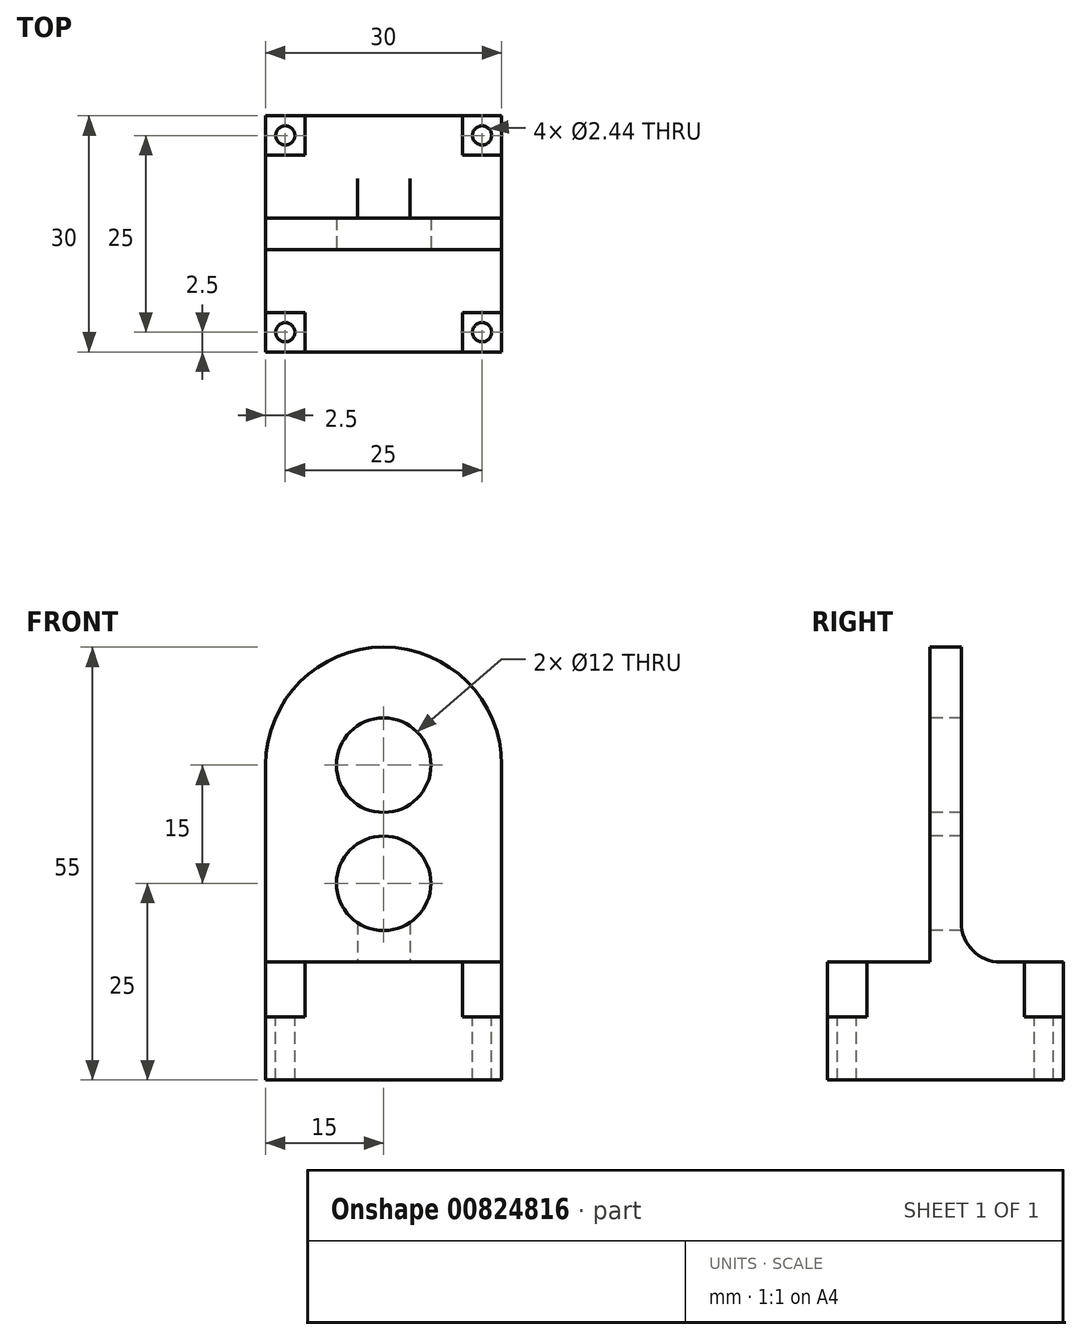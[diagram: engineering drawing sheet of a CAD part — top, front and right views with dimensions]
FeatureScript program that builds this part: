
annotation { "Feature Type Name" : "Feature", "Feature Type Description" : "" }
export const myFeature = defineFeature(function(context is Context, id is Id, definition is map)
    precondition{}
    {
        {
            var Q0;
            Q0=qCreatedBy(makeId("Top.planeOp"),FACE);
            var sketch = newSketch(context, id + "F0", { "sketchPlane" : qUnion([Q0])});
            skLineSegment(sketch, "E0.bottom", {"start": v(15, -15) * mm, "end": v(-15, -15) * mm});
            skLineSegment(sketch, "E0.top", {"start": v(15, 15) * mm, "end": v(-15, 15) * mm});
            skLineSegment(sketch, "E0.left", {"start": v(15, -15) * mm, "end": v(15, 15) * mm});
            skLineSegment(sketch, "E0.right", {"start": v(-15, -15) * mm, "end": v(-15, 15) * mm});
            skPoint(sketch, "E0.middle", {"position": v(0, 0) * mm});
            skSolve(sketch);
        }
        {
            var Q0;
            Q0=makeQuery(id+"F0.imprint","IMPRINT",FACE,{"disambiguationData":[TD([[makeQuery(id+"F0.imprint","IMPRINT",EDGE,{"derivedFrom":sQuery(id+"F0.wireOp",EDGE,"E0.bottom")}),-1.0]])]});
            extrude(context, id + "F1", {"entities" : qUnion([Q0]), "depth" : 15 * mm, "offsetDistance" : 25 * mm});
        }
        {
            var Q0;
            Q0=makeQuery(id+"F1.opExtrude","CAP_FACE",FACE,{"disambiguationData":[OSD([sQuery(id+"F0.wireOp",EDGE,"E0.bottom"),sQuery(id+"F0.wireOp",EDGE,"E0.top"),sQuery(id+"F0.wireOp",EDGE,"E0.left"),sQuery(id+"F0.wireOp",EDGE,"E0.right")])],"isStart":false});
            var sketch = newSketch(context, id + "F2", { "sketchPlane" : qUnion([Q0])});
            skLineSegment(sketch, "E1.bottom", {"start": v(-15, 15) * mm, "end": v(-10, 15) * mm});
            skLineSegment(sketch, "E1.top", {"start": v(-15, 10) * mm, "end": v(-10, 10) * mm});
            skLineSegment(sketch, "E1.left", {"start": v(-15, 15) * mm, "end": v(-15, 10) * mm});
            skLineSegment(sketch, "E1.right", {"start": v(-10, 15) * mm, "end": v(-10, 10) * mm});
            skLineSegment(sketch, "E2.bottom", {"start": v(15, 15) * mm, "end": v(10, 15) * mm});
            skLineSegment(sketch, "E2.top", {"start": v(15, 10) * mm, "end": v(10, 10) * mm});
            skLineSegment(sketch, "E2.left", {"start": v(15, 15) * mm, "end": v(15, 10) * mm});
            skLineSegment(sketch, "E2.right", {"start": v(10, 15) * mm, "end": v(10, 10) * mm});
            skLineSegment(sketch, "E3.bottom", {"start": v(15, -15) * mm, "end": v(10, -15) * mm});
            skLineSegment(sketch, "E3.top", {"start": v(15, -10) * mm, "end": v(10, -10) * mm});
            skLineSegment(sketch, "E3.left", {"start": v(15, -15) * mm, "end": v(15, -10) * mm});
            skLineSegment(sketch, "E3.right", {"start": v(10, -15) * mm, "end": v(10, -10) * mm});
            skLineSegment(sketch, "E4.bottom", {"start": v(-15, -15) * mm, "end": v(-10, -15) * mm});
            skLineSegment(sketch, "E4.top", {"start": v(-15, -10) * mm, "end": v(-10, -10) * mm});
            skLineSegment(sketch, "E4.left", {"start": v(-15, -15) * mm, "end": v(-15, -10) * mm});
            skLineSegment(sketch, "E4.right", {"start": v(-10, -15) * mm, "end": v(-10, -10) * mm});
            skSolve(sketch);
        }
        {
            var Q0;
            Q0=makeQuery(id+"F2.imprint","IMPRINT",FACE,{"disambiguationData":[TD([[makeQuery(id+"F2.imprint","IMPRINT",EDGE,{"derivedFrom":sQuery(id+"F2.wireOp",EDGE,"E1.bottom")}),1.0]])]});
            var Q1;
            Q1=makeQuery(id+"F2.imprint","IMPRINT",FACE,{"disambiguationData":[TD([[makeQuery(id+"F2.imprint","IMPRINT",EDGE,{"derivedFrom":sQuery(id+"F2.wireOp",EDGE,"E2.bottom")}),1.0]])]});
            var Q2;
            Q2=makeQuery(id+"F2.imprint","IMPRINT",FACE,{"disambiguationData":[TD([[makeQuery(id+"F2.imprint","IMPRINT",EDGE,{"derivedFrom":sQuery(id+"F2.wireOp",EDGE,"E3.bottom")}),-1.0]])]});
            var Q3;
            Q3=makeQuery(id+"F2.imprint","IMPRINT",FACE,{"disambiguationData":[TD([[makeQuery(id+"F2.imprint","IMPRINT",EDGE,{"derivedFrom":sQuery(id+"F2.wireOp",EDGE,"E4.bottom")}),-1.0]])]});
            extrude(context, id + "F3", {"entities" : qUnion([Q0, Q1, Q2, Q3]), "operationType" : NewBodyOperationType.REMOVE, "oppositeDirection" : true, "depth" : 7 * mm, "offsetDistance" : 25 * mm});
        }
        {
            var Q0;
            Q0=makeQuery(id+"F3.boolean.opBoolean","COPY",FACE,{"derivedFrom":makeQuery(id+"F3.opExtrude","CAP_FACE",FACE,{"disambiguationData":[OSD([sQuery(id+"F2.wireOp",EDGE,"E1.bottom"),sQuery(id+"F2.wireOp",EDGE,"E1.top"),sQuery(id+"F2.wireOp",EDGE,"E1.left"),sQuery(id+"F2.wireOp",EDGE,"E1.right")])],"isStart":false})});
            var sketch = newSketch(context, id + "F4", { "sketchPlane" : qUnion([Q0])});
            skCircle(sketch, "E5", {"center": v(-12.5, 12.5) * mm, "radius": 1.22 * mm});
            skPoint(sketch, "E5.centerSnap0", {"position": v(-12.5, 15) * mm});
            skPoint(sketch, "E5.centerSnap1", {"position": v(-15, 12.5) * mm});
            skCircle(sketch, "E6.1.0", {"center": v(-12.5, -12.5) * mm, "radius": 1.22 * mm});
            skCircle(sketch, "E6.2.0", {"center": v(12.5, -12.5) * mm, "radius": 1.22 * mm});
            skCircle(sketch, "E6.3.0", {"center": v(12.5, 12.5) * mm, "radius": 1.22 * mm});
            skPoint(sketch, "E6.center", {"position": v(0, 0) * mm});
            skSolve(sketch);
        }
        {
            var Q0;
            Q0=makeQuery(id+"F4.imprint","IMPRINT",FACE,{"disambiguationData":[TD([[makeQuery(id+"F4.imprint","IMPRINT",EDGE,{"derivedFrom":sQuery(id+"F4.wireOp",EDGE,"E5")}),1.0]])]});
            var Q1;
            Q1=makeQuery(id+"F4.imprint","IMPRINT",FACE,{"disambiguationData":[TD([[makeQuery(id+"F4.imprint","IMPRINT",EDGE,{"derivedFrom":sQuery(id+"F4.wireOp",EDGE,"E6.3.0")}),1.0]])]});
            var Q2;
            Q2=makeQuery(id+"F4.imprint","IMPRINT",FACE,{"disambiguationData":[TD([[makeQuery(id+"F4.imprint","IMPRINT",EDGE,{"derivedFrom":sQuery(id+"F4.wireOp",EDGE,"E6.2.0")}),1.0]])]});
            var Q3;
            Q3=makeQuery(id+"F4.imprint","IMPRINT",FACE,{"disambiguationData":[TD([[makeQuery(id+"F4.imprint","IMPRINT",EDGE,{"derivedFrom":sQuery(id+"F4.wireOp",EDGE,"E6.1.0")}),1.0]])]});
            extrude(context, id + "F5", {"entities" : qUnion([Q0, Q1, Q2, Q3]), "operationType" : NewBodyOperationType.REMOVE, "endBound" : BoundingType.THROUGH_ALL, "oppositeDirection" : true, "depth" : 25 * mm, "offsetDistance" : 25 * mm});
        }
        {
            var Q0;
            Q0=qCreatedBy(makeId("Front.planeOp"),FACE);
            var sketch = newSketch(context, id + "F6", { "sketchPlane" : qUnion([Q0])});
            skLineSegment(sketch, "E7.bottom", {"start": v(-15, 15) * mm, "end": v(15, 15) * mm});
            skLineSegment(sketch, "E7.top", {"start": v(0, 55) * mm, "end": v(0, 55) * mm});
            skLineSegment(sketch, "E7.left", {"start": v(-15, 15) * mm, "end": v(-15, 40) * mm});
            skLineSegment(sketch, "E7.right", {"start": v(15, 15) * mm, "end": v(15, 40) * mm});
            skPoint(sketch, "E8.visualSharp", {"position": v(-15, 55) * mm});
            skArc(sketch, "E8.filletArc", {"start": v(0, 55) * mm, "mid": v(-10.6, 50.6) * mm, "end": v(-15, 40) * mm});
            skPoint(sketch, "E9.visualSharp", {"position": v(15, 55) * mm});
            skArc(sketch, "E9.filletArc", {"start": v(15, 40) * mm, "mid": v(10.6, 50.6) * mm, "end": v(0, 55) * mm});
            skSolve(sketch);
        }
        {
            var Q0;
            Q0=makeQuery(id+"F6.imprint","IMPRINT",FACE,{"disambiguationData":[TD([[makeQuery(id+"F6.imprint","IMPRINT",EDGE,{"derivedFrom":sQuery(id+"F6.wireOp",EDGE,"E7.bottom")}),1.0]])]});
            extrude(context, id + "F7", {"entities" : qUnion([Q0]), "operationType" : NewBodyOperationType.ADD, "endBound" : BoundingType.SYMMETRIC, "depth" : 4 * mm, "offsetDistance" : 25 * mm});
        }
        {
            var Q0;
            Q0=makeQuery(id+"F7.opExtrude","CAP_FACE",FACE,{"disambiguationData":[OSD([sQuery(id+"F6.wireOp",EDGE,"E7.bottom"),sQuery(id+"F6.wireOp",EDGE,"E7.left"),sQuery(id+"F6.wireOp",EDGE,"E7.right"),sQuery(id+"F6.wireOp",EDGE,"E8.filletArc"),sQuery(id+"F6.wireOp",EDGE,"E9.filletArc")])],"isStart":false});
            var sketch = newSketch(context, id + "F8", { "sketchPlane" : qUnion([Q0])});
            skCircle(sketch, "E10", {"center": v(0, 40) * mm, "radius": 6 * mm});
            skCircle(sketch, "E11", {"center": v(0, 25) * mm, "radius": 6 * mm});
            skSolve(sketch);
        }
        {
            var Q0;
            Q0=makeQuery(id+"F8.imprint","IMPRINT",FACE,{"disambiguationData":[TD([[makeQuery(id+"F8.imprint","IMPRINT",EDGE,{"derivedFrom":sQuery(id+"F8.wireOp",EDGE,"E10")}),1.0]])]});
            var Q1;
            Q1=makeQuery(id+"F8.imprint","IMPRINT",FACE,{"disambiguationData":[TD([[makeQuery(id+"F8.imprint","IMPRINT",EDGE,{"derivedFrom":sQuery(id+"F8.wireOp",EDGE,"E11")}),1.0]])]});
            extrude(context, id + "F9", {"entities" : qUnion([Q0, Q1]), "operationType" : NewBodyOperationType.REMOVE, "endBound" : BoundingType.THROUGH_ALL, "oppositeDirection" : true, "depth" : 25 * mm, "offsetDistance" : 25 * mm});
        }
        {
            var Q0;
            Q0=makeQuery(id+"F7.opExtrude","CAP_EDGE",EDGE,{"disambiguationData":[OSD([sQuery(id+"F6.wireOp",EDGE,"E7.bottom")])],"isStart":false});
            var Q1;
            Q1=makeQuery(id+"F7.opExtrude","CAP_EDGE",EDGE,{"disambiguationData":[OSD([sQuery(id+"F6.wireOp",EDGE,"E7.bottom")])],"isStart":true});
            fillet(context, id + "F10", {"entities" : qUnion([Q0, Q1]), "radius" : 5 * mm, "tangentPropagation" : true, "allowEdgeOverflow" : false});
        }
    });
